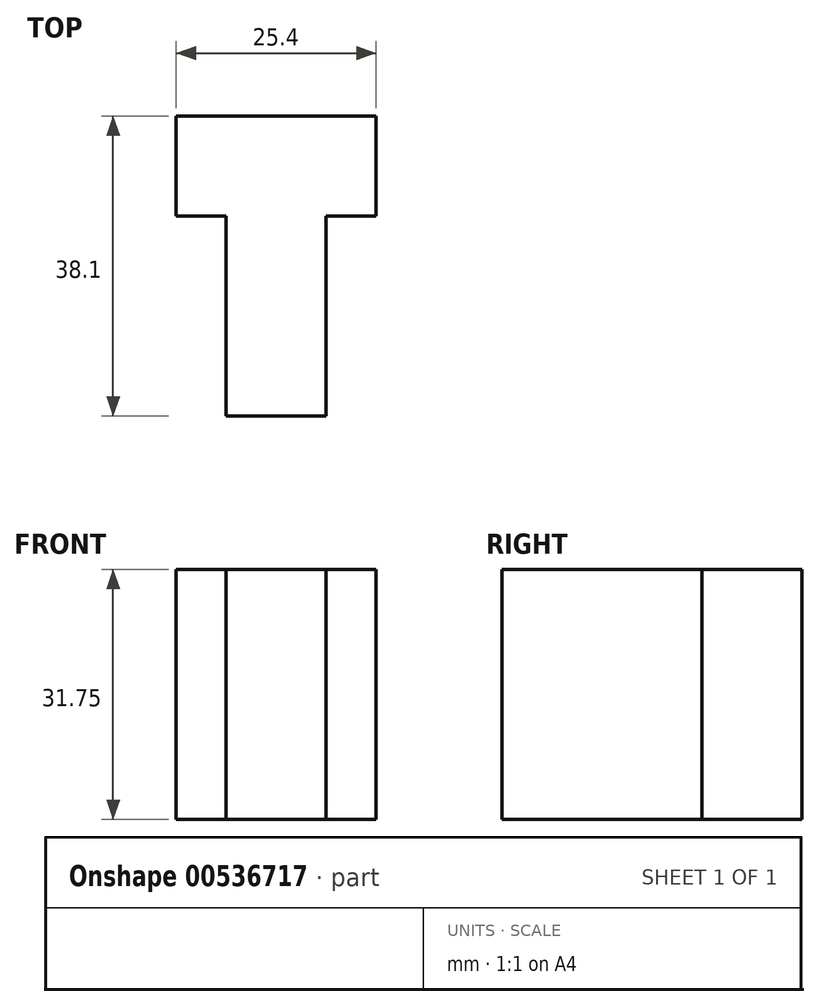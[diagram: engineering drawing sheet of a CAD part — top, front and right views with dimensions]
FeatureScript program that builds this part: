
annotation { "Feature Type Name" : "Feature", "Feature Type Description" : "" }
export const myFeature = defineFeature(function(context is Context, id is Id, definition is map)
    precondition{}
    {
        {
            var Q0;
            Q0=qCreatedBy(makeId("Top.planeOp"),FACE);
            var sketch = newSketch(context, id + "F0", { "sketchPlane" : qUnion([Q0])});
            skLineSegment(sketch, "E0.bottom", {"start": v(-25.4, 38.1) * mm, "end": v(0, 38.1) * mm});
            skLineSegment(sketch, "E0.top", {"start": v(-25.4, 25.4) * mm, "end": v(0, 25.4) * mm});
            skLineSegment(sketch, "E0.left", {"start": v(-25.4, 38.1) * mm, "end": v(-25.4, 25.4) * mm});
            skLineSegment(sketch, "E0.right", {"start": v(0, 38.1) * mm, "end": v(0, 25.4) * mm});
            skLineSegment(sketch, "E1.bottom", {"start": v(-19.05, 25.4) * mm, "end": v(-6.35, 25.4) * mm});
            skLineSegment(sketch, "E1.top", {"start": v(-19.05, 0) * mm, "end": v(-6.35, 0) * mm});
            skLineSegment(sketch, "E1.left", {"start": v(-19.05, 25.4) * mm, "end": v(-19.05, 0) * mm});
            skLineSegment(sketch, "E1.right", {"start": v(-6.35, 25.4) * mm, "end": v(-6.35, 0) * mm});
            skSolve(sketch);
        }
        {
            var Q0;
            Q0 = qSketchRegion(id + "F0", true);
            extrude(context, id + "F1", {"entities" : qUnion([Q0]), "depth" : 31.75 * mm, "offsetDistance" : 25.4 * mm});
        }
    });
